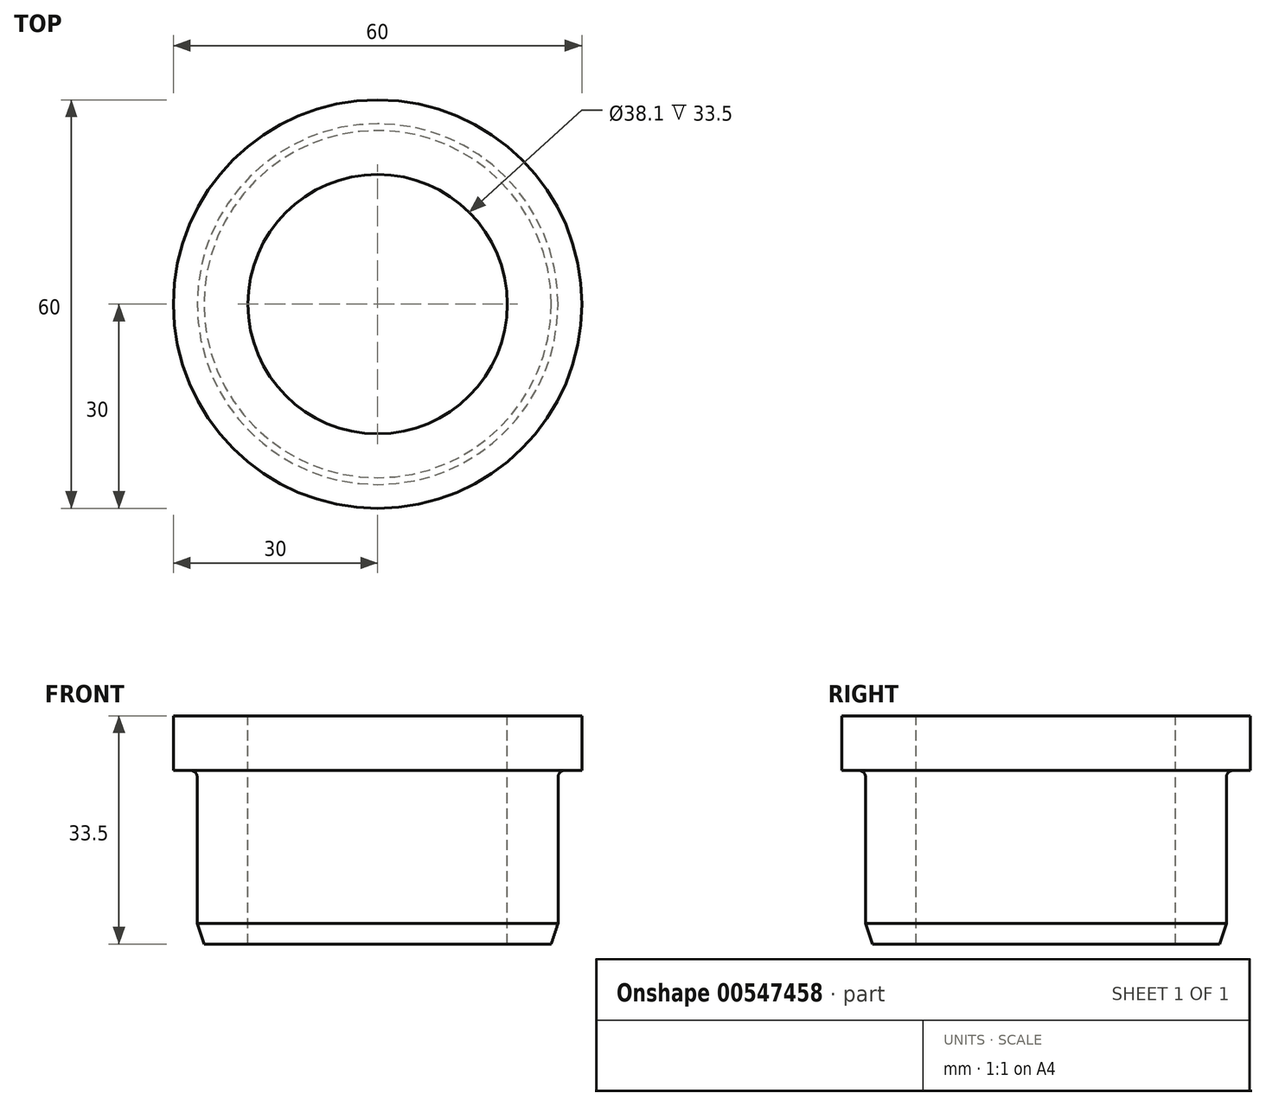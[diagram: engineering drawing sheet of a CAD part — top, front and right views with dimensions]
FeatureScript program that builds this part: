
annotation { "Feature Type Name" : "Feature", "Feature Type Description" : "" }
export const myFeature = defineFeature(function(context is Context, id is Id, definition is map)
    precondition{}
    {
        {
            var Q0;
            Q0=qCreatedBy(makeId("Front.planeOp"),FACE);
            var sketch = newSketch(context, id + "F0", { "sketchPlane" : qUnion([Q0])});
            skLineSegment(sketch, "E0", {"start": v(0, 50.08) * mm, "end": v(0, -44.4) * mm, "construction": true});
            skLineSegment(sketch, "E1", {"start": v(-30, 16.75) * mm, "end": v(-19.05, 16.75) * mm});
            skLineSegment(sketch, "E2", {"start": v(-19.05, 16.75) * mm, "end": v(-19.05, -16.75) * mm});
            skLineSegment(sketch, "E3", {"start": v(-19.05, -16.75) * mm, "end": v(-26.5, -16.75) * mm});
            skLineSegment(sketch, "E4", {"start": v(-26.5, -16.75) * mm, "end": v(-26.5, 8.75) * mm});
            skLineSegment(sketch, "E5", {"start": v(-26.5, 8.75) * mm, "end": v(-30, 8.75) * mm});
            skLineSegment(sketch, "E6", {"start": v(-30, 8.75) * mm, "end": v(-30, 16.75) * mm});
            skSolve(sketch);
        }
        {
            var Q0;
            Q0=makeQuery(id+"F0.imprint","IMPRINT",FACE,{"disambiguationData":[TD([[makeQuery(id+"F0.imprint","IMPRINT",EDGE,{"derivedFrom":sQuery(id+"F0.wireOp",EDGE,"E1")}),-1.0]])]});
            var Q1;
            Q1=sQuery(id+"F0.wireOp",EDGE,"E0");
            revolve(context, id + "F1", {"entities" : qUnion([Q0]), "axis" : qUnion([Q1]), "revolveType" : RevolveType.FULL});
        }
        {
            var Q0;
            Q0=makeQuery(id+"F1.opRevolve","SWEPT_EDGE",EDGE,{"disambiguationData":[OSD([sQuery(id+"F0.wireOp",EDGE,"E3"),sQuery(id+"F0.wireOp",EDGE,"E4")])]});
            chamfer(context, id + "F2", {"entities" : qUnion([Q0]), "chamferType" : ChamferType.TWO_OFFSETS, "width1" : 3 * mm, "oppositeDirection" : false, "width2" : 1 * mm, "tangentPropagation" : true});
        }
        {
            var Q0;
            Q0=makeQuery(id+"F1.opRevolve","SWEPT_EDGE",EDGE,{"disambiguationData":[OSD([sQuery(id+"F0.wireOp",EDGE,"E4"),sQuery(id+"F0.wireOp",EDGE,"E5")])]});
            fillet(context, id + "F3", {"entities" : qUnion([Q0]), "radius" : 1 * mm, "tangentPropagation" : true, "allowEdgeOverflow" : false});
        }
    });
